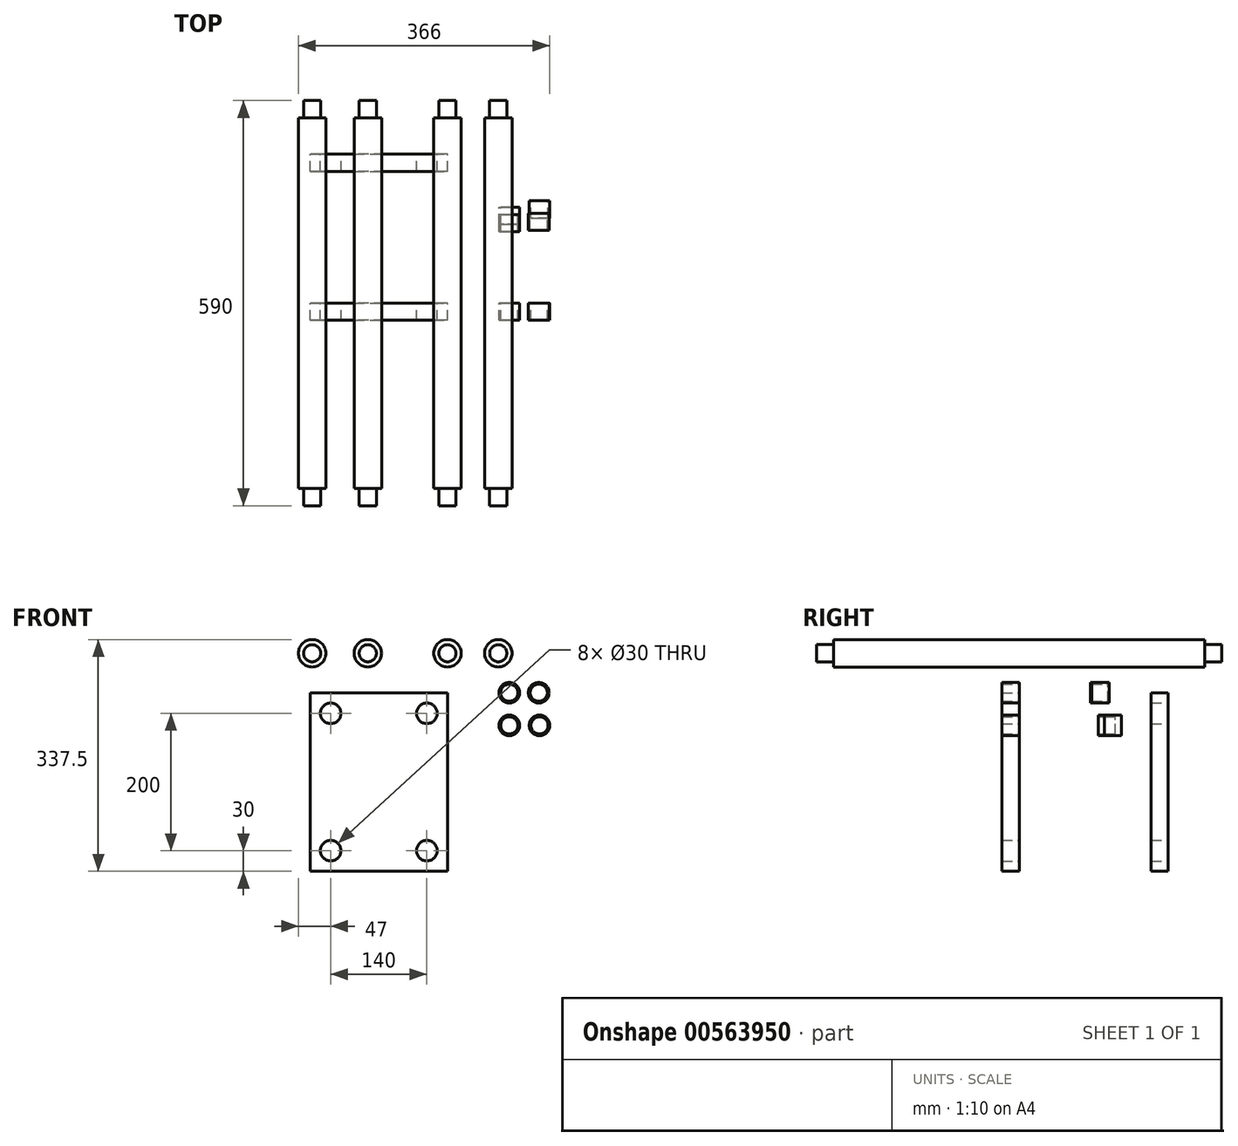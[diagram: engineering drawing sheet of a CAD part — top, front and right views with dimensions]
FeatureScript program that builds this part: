
annotation { "Feature Type Name" : "Feature", "Feature Type Description" : "" }
export const myFeature = defineFeature(function(context is Context, id is Id, definition is map)
    precondition{}
    {
        {
            var Q0;
            Q0=qCreatedBy(makeId("Front.planeOp"),FACE);
            var sketch = newSketch(context, id + "F0", { "sketchPlane" : qUnion([Q0])});
            skLineSegment(sketch, "E0", {"start": v(0, 0) * mm, "end": v(0, -260) * mm});
            skLineSegment(sketch, "E1", {"start": v(0, -260) * mm, "end": v(-200, -260) * mm});
            skLineSegment(sketch, "E2", {"start": v(-200, -260) * mm, "end": v(-200, 0) * mm});
            skCircle(sketch, "E3", {"center": v(-170, -230) * mm, "radius": 15 * mm});
            skCircle(sketch, "E4", {"center": v(-30, -230) * mm, "radius": 15 * mm});
            skCircle(sketch, "E5", {"center": v(-170, -30) * mm, "radius": 15 * mm});
            skCircle(sketch, "E6", {"center": v(-30, -30) * mm, "radius": 15 * mm});
            skLineSegment(sketch, "E7", {"start": v(-200, 0) * mm, "end": v(0, 0) * mm});
            skSolve(sketch);
        }
        {
            var Q0;
            Q0=makeQuery(id+"F0.imprint","IMPRINT",FACE,{"disambiguationData":[TD([[makeQuery(id+"F0.imprint","IMPRINT",EDGE,{"derivedFrom":sQuery(id+"F0.wireOp",EDGE,"E0")}),-1.0]])]});
            extrude(context, id + "F1", {"entities" : qUnion([Q0]), "depth" : 25 * mm, "offsetDistance" : 25 * mm});
        }
        {
            var Q0;
            Q0=qCreatedBy(makeId("Front.planeOp"),FACE);
            var sketch = newSketch(context, id + "F2", { "sketchPlane" : qUnion([Q0])});
            skCircle(sketch, "E8", {"center": v(90, 0) * mm, "radius": 15 * mm});
            skCircle(sketch, "E9", {"center": v(90, 0) * mm, "radius": 12.5 * mm});
            skSolve(sketch);
        }
        {
            var Q0;
            Q0=makeQuery(id+"F2.imprint","IMPRINT",FACE,{"disambiguationData":[TD([[makeQuery(id+"F2.imprint","IMPRINT",EDGE,{"derivedFrom":sQuery(id+"F2.wireOp",EDGE,"E8")}),1.0]])]});
            extrude(context, id + "F3", {"entities" : qUnion([Q0]), "depth" : 25 * mm, "offsetDistance" : 25 * mm});
        }
        {
            var Q0;
            Q0=makeQuery(id+"F3.opExtrude","SWEPT_BODY",BODY,{"disambiguationData":[OSD([sQuery(id+"F2.wireOp",EDGE,"E8"),sQuery(id+"F2.wireOp",EDGE,"E9")])]});
            transform(context, id + "F4", {"entities" : qUnion([Q0]), "transformType" : TransformType.TRANSLATION_3D, "dx" : 42.9 * mm, "dy" : 0 * mm, "dz" : 0 * mm, "makeCopy" : true});
        }
        {
            var Q0;
            Q0=makeQuery(id+"F3.opExtrude","SWEPT_BODY",BODY,{"disambiguationData":[OSD([sQuery(id+"F2.wireOp",EDGE,"E8"),sQuery(id+"F2.wireOp",EDGE,"E9")])]});
            transform(context, id + "F5", {"entities" : qUnion([Q0]), "transformType" : TransformType.TRANSLATION_3D, "dx" : 0 * mm, "dy" : 0 * mm, "dz" : -47.6 * mm, "makeCopy" : true});
        }
        {
            var Q0;
            Q0=makeQuery(id+"F5.opPattern","COPY",BODY,{"derivedFrom":makeQuery(id+"F3.opExtrude","SWEPT_BODY",BODY,{"disambiguationData":[OSD([sQuery(id+"F2.wireOp",EDGE,"E8"),sQuery(id+"F2.wireOp",EDGE,"E9")])]}),"instanceName":"1"});
            transform(context, id + "F6", {"entities" : qUnion([Q0]), "transformType" : TransformType.TRANSLATION_3D, "dx" : 44 * mm, "dy" : 0 * mm, "dz" : 0 * mm, "makeCopy" : true});
        }
        {
            var Q0;
            Q0=makeQuery(id+"F1.opExtrude","SWEPT_BODY",BODY,{"disambiguationData":[OSD([sQuery(id+"F0.wireOp",EDGE,"E0"),sQuery(id+"F0.wireOp",EDGE,"E1"),sQuery(id+"F0.wireOp",EDGE,"E2"),sQuery(id+"F0.wireOp",EDGE,"E3"),sQuery(id+"F0.wireOp",EDGE,"E4"),sQuery(id+"F0.wireOp",EDGE,"E5"),sQuery(id+"F0.wireOp",EDGE,"E6"),sQuery(id+"F0.wireOp",EDGE,"E7")])]});
            transform(context, id + "F7", {"entities" : qUnion([Q0]), "transformType" : TransformType.TRANSLATION_3D, "dx" : 0 * mm, "dy" : 217 * mm, "dz" : 0 * mm, "makeCopy" : true});
        }
        {
            var Q0;
            Q0=makeQuery(id+"F3.opExtrude","SWEPT_BODY",BODY,{"disambiguationData":[OSD([sQuery(id+"F2.wireOp",EDGE,"E8"),sQuery(id+"F2.wireOp",EDGE,"E9")])]});
            transform(context, id + "F8", {"entities" : qUnion([Q0]), "transformType" : TransformType.TRANSLATION_3D, "dx" : 0 * mm, "dy" : 129 * mm, "dz" : 0 * mm, "makeCopy" : true});
        }
        {
            var Q0;
            Q0=makeQuery(id+"F4.opPattern","COPY",BODY,{"derivedFrom":makeQuery(id+"F3.opExtrude","SWEPT_BODY",BODY,{"disambiguationData":[OSD([sQuery(id+"F2.wireOp",EDGE,"E8"),sQuery(id+"F2.wireOp",EDGE,"E9")])]}),"instanceName":"1"});
            transform(context, id + "F9", {"entities" : qUnion([Q0]), "transformType" : TransformType.TRANSLATION_3D, "dx" : 0 * mm, "dy" : 131 * mm, "dz" : 0 * mm, "makeCopy" : true});
        }
        {
            var Q0;
            Q0=makeQuery(id+"F5.opPattern","COPY",BODY,{"derivedFrom":makeQuery(id+"F3.opExtrude","SWEPT_BODY",BODY,{"disambiguationData":[OSD([sQuery(id+"F2.wireOp",EDGE,"E8"),sQuery(id+"F2.wireOp",EDGE,"E9")])]}),"instanceName":"1"});
            transform(context, id + "F10", {"entities" : qUnion([Q0]), "transformType" : TransformType.TRANSLATION_3D, "dx" : 0 * mm, "dy" : 140 * mm, "dz" : 0 * mm, "makeCopy" : true});
        }
        {
            var Q0;
            Q0=makeQuery(id+"F6.opPattern","COPY",BODY,{"derivedFrom":makeQuery(id+"F5.opPattern","COPY",BODY,{"derivedFrom":makeQuery(id+"F3.opExtrude","SWEPT_BODY",BODY,{"disambiguationData":[OSD([sQuery(id+"F2.wireOp",EDGE,"E8"),sQuery(id+"F2.wireOp",EDGE,"E9")])]}),"instanceName":"1"}),"instanceName":"1"});
            transform(context, id + "F11", {"entities" : qUnion([Q0]), "transformType" : TransformType.TRANSLATION_3D, "dx" : 0 * mm, "dy" : 149 * mm, "dz" : 0 * mm, "makeCopy" : true});
        }
        {
            var Q0;
            Q0=qCreatedBy(makeId("Front.planeOp"),FACE);
            var sketch = newSketch(context, id + "F12", { "sketchPlane" : qUnion([Q0])});
            skCircle(sketch, "E10", {"center": v(0, 57.5) * mm, "radius": 20 * mm});
            skCircle(sketch, "E11", {"center": v(0, 57.5) * mm, "radius": 12.5 * mm});
            skSolve(sketch);
        }
        {
            var Q0;
            Q0=makeQuery(id+"F12.imprint","IMPRINT",FACE,{"disambiguationData":[TD([[makeQuery(id+"F12.imprint","IMPRINT",EDGE,{"derivedFrom":sQuery(id+"F12.wireOp",EDGE,"E11")}),1.0]])]});
            extrude(context, id + "F13", {"entities" : qUnion([Q0]), "endBound" : BoundingType.SYMMETRIC, "depth" : 590 * mm, "offsetDistance" : 25 * mm});
        }
        {
            var Q0;
            Q0=qSketchRegion(id+"F12",true);
            extrude(context, id + "F14", {"entities" : qUnion([Q0]), "operationType" : NewBodyOperationType.ADD, "endBound" : BoundingType.SYMMETRIC, "depth" : 540 * mm, "offsetDistance" : 25 * mm});
        }
        {
            var Q0;
            Q0=makeQuery(id+"F13.opExtrude","SWEPT_BODY",BODY,{"disambiguationData":[OSD([sQuery(id+"F12.wireOp",EDGE,"E11")])]});
            transform(context, id + "F15", {"entities" : qUnion([Q0]), "transformType" : TransformType.TRANSLATION_3D, "dx" : 74 * mm, "dy" : 0 * mm, "dz" : 0 * mm, "makeCopy" : true});
        }
        {
            var Q0;
            Q0=makeQuery(id+"F13.opExtrude","SWEPT_BODY",BODY,{"disambiguationData":[OSD([sQuery(id+"F12.wireOp",EDGE,"E11")])]});
            transform(context, id + "F16", {"entities" : qUnion([Q0]), "transformType" : TransformType.TRANSLATION_3D, "dx" : -116 * mm, "dy" : 0 * mm, "dz" : 0 * mm, "makeCopy" : true});
        }
        {
            var Q0;
            Q0=makeQuery(id+"F16.opPattern","COPY",BODY,{"derivedFrom":makeQuery(id+"F13.opExtrude","SWEPT_BODY",BODY,{"disambiguationData":[OSD([sQuery(id+"F12.wireOp",EDGE,"E11")])]}),"instanceName":"1"});
            transform(context, id + "F17", {"entities" : qUnion([Q0]), "transformType" : TransformType.TRANSLATION_3D, "dx" : -81 * mm, "dy" : 0 * mm, "dz" : 0 * mm, "makeCopy" : true});
        }
    });
